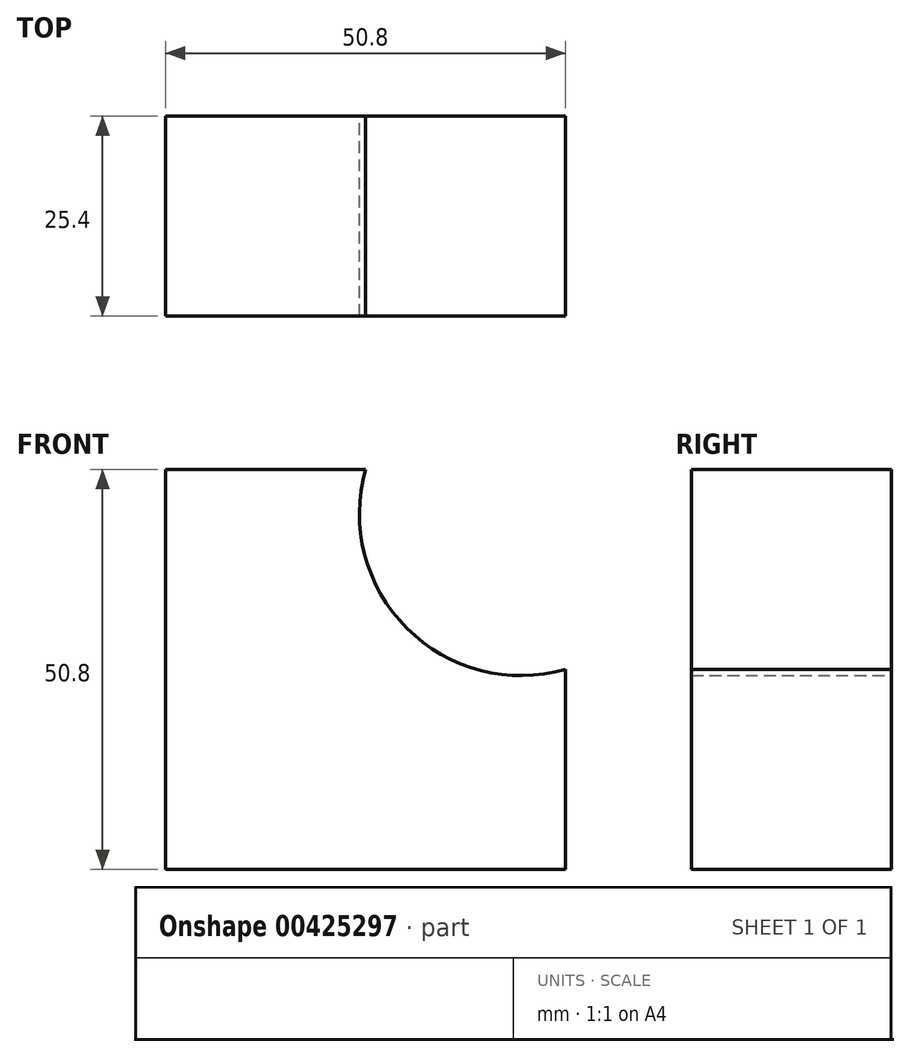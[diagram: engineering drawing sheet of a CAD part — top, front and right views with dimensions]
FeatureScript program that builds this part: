
annotation { "Feature Type Name" : "Feature", "Feature Type Description" : "" }
export const myFeature = defineFeature(function(context is Context, id is Id, definition is map)
    precondition{}
    {
        {
            var Q0;
            Q0=qCreatedBy(makeId("Front.planeOp"),FACE);
            var sketch = newSketch(context, id + "F0", { "sketchPlane" : qUnion([Q0])});
            skLineSegment(sketch, "E0", {"start": v(0, 0) * mm, "end": v(-50.8, 0) * mm});
            skLineSegment(sketch, "E1", {"start": v(-50.8, 0) * mm, "end": v(-50.8, 50.8) * mm});
            skLineSegment(sketch, "E2", {"start": v(-50.8, 50.8) * mm, "end": v(-25.4, 50.8) * mm});
            skLineSegment(sketch, "E3", {"start": v(0, 0) * mm, "end": v(0, 25.4) * mm});
            skArc(sketch, "E4", {"start": v(-25.4, 50.8) * mm, "mid": v(-20.16, 30.64) * mm, "end": v(0, 25.4) * mm});
            skSolve(sketch);
        }
        {
            var Q0;
            Q0 = qSketchRegion(id + "F0", true);
            extrude(context, id + "F1", {"entities" : qUnion([Q0]), "depth" : 25.4 * mm});
        }
    });
